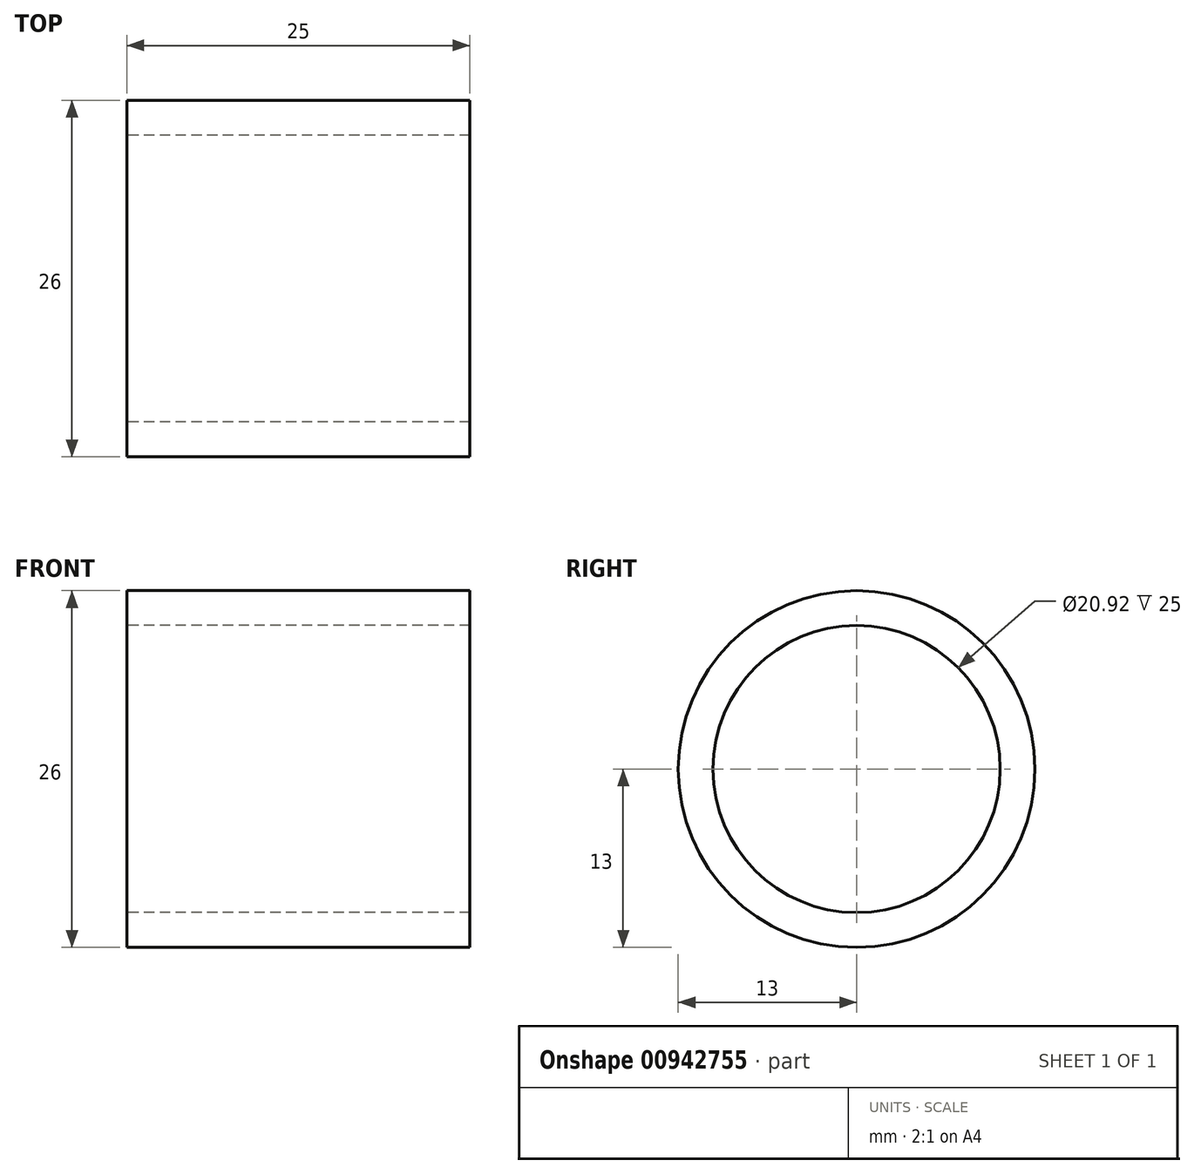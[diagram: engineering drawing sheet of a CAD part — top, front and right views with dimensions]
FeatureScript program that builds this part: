
annotation { "Feature Type Name" : "Feature", "Feature Type Description" : "" }
export const myFeature = defineFeature(function(context is Context, id is Id, definition is map)
    precondition{}
    {
        {
            var Q0;
            Q0=qCreatedBy(makeId("Right.planeOp"),FACE);
            var sketch = newSketch(context, id + "F0", { "sketchPlane" : qUnion([Q0])});
            skCircle(sketch, "E0", {"center": v(0, 0) * mm, "radius": 13 * mm});
            skCircle(sketch, "E1", {"center": v(0, 0) * mm, "radius": 10.46 * mm});
            skSolve(sketch);
        }
        {
            var Q0;
            Q0=makeQuery(id+"F0.imprint","IMPRINT",FACE,{"disambiguationData":[TD([[makeQuery(id+"F0.imprint","IMPRINT",EDGE,{"derivedFrom":sQuery(id+"F0.wireOp",EDGE,"E0")}),1.0]])]});
            extrude(context, id + "F1", {"entities" : qUnion([Q0]), "depth" : 25 * mm, "offsetDistance" : 25.4 * mm});
        }
    });
